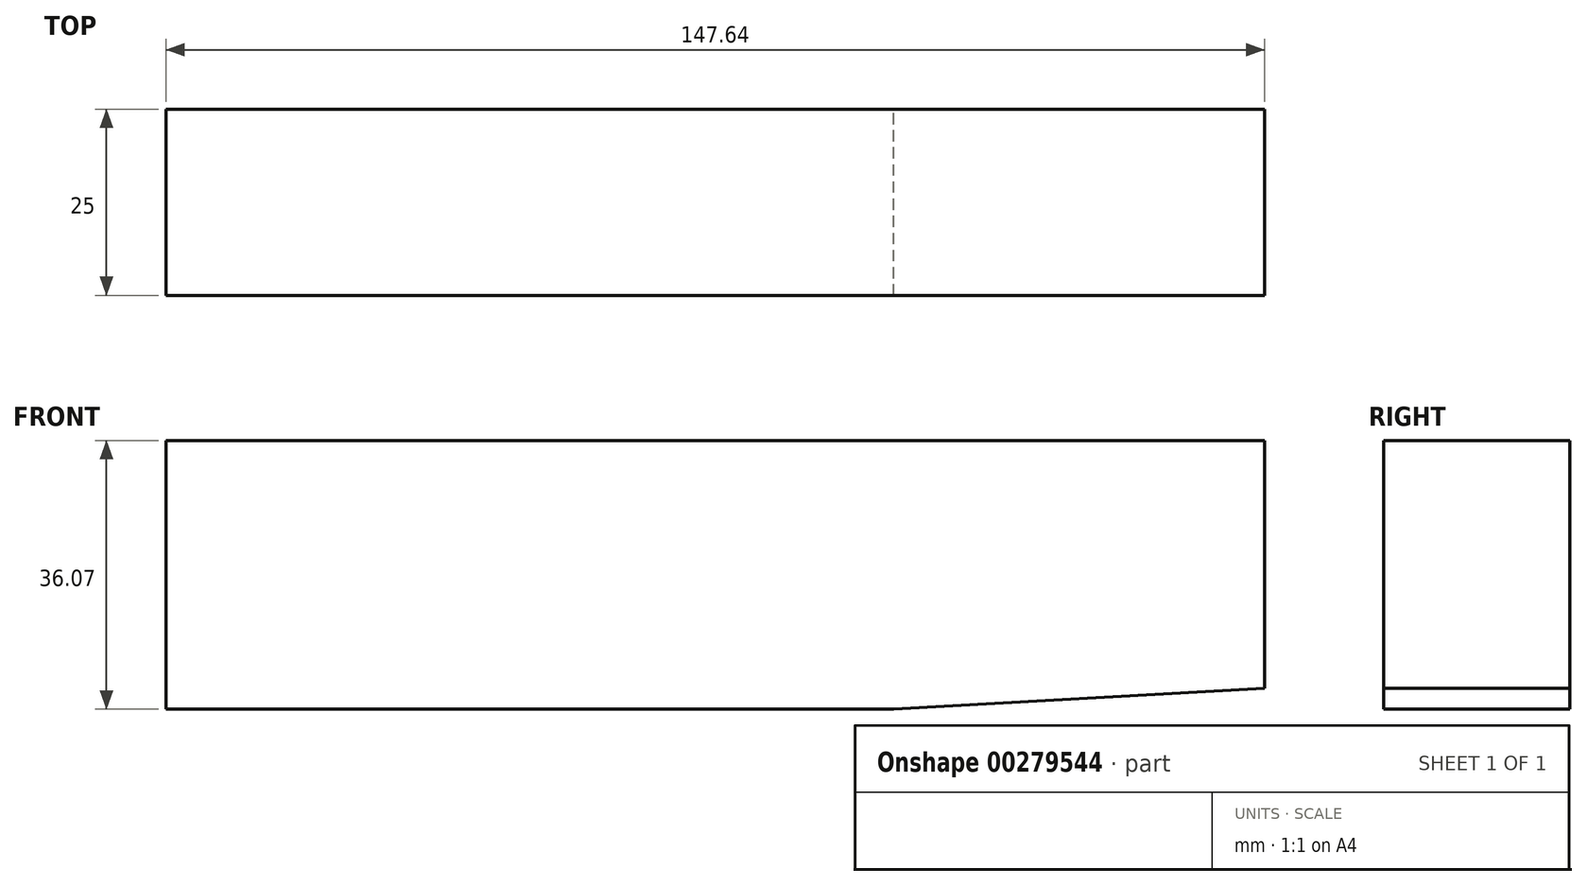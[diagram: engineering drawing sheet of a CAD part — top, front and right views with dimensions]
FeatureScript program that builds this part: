
annotation { "Feature Type Name" : "Feature", "Feature Type Description" : "" }
export const myFeature = defineFeature(function(context is Context, id is Id, definition is map)
    precondition{}
    {
        {
            var Q0;
            Q0=qCreatedBy(makeId("Front.planeOp"),FACE);
            var sketch = newSketch(context, id + "F0", { "sketchPlane" : qUnion([Q0])});
            skLineSegment(sketch, "E0", {"start": v(-10.57, 42.69) * mm, "end": v(40.71, 42.69) * mm});
            skLineSegment(sketch, "E1", {"start": v(40.71, 42.69) * mm, "end": v(40.71, 9.44) * mm});
            skLineSegment(sketch, "E2", {"start": v(40.71, 9.44) * mm, "end": v(-9.16, 6.62) * mm});
            skLineSegment(sketch, "E3", {"start": v(-9.16, 6.62) * mm, "end": v(-9.16, 42.69) * mm});
            skSolve(sketch);
        }
        {
            var Q0;
            {var subQ0=sQuery(id+"F0.wireOp",EDGE,"E1");Q0=makeQuery(id+"F0.imprint","IMPRINT",FACE,{"disambiguationData":[TD([[makeQuery(id+"F0.imprint","IMPRINT",EDGE,{"derivedFrom":subQ0}),-1.0]])]});}
            extrude(context, id + "F1", {"entities" : qUnion([Q0]), "depth" : 25 * mm});
        }
        {
            var Q0;
            Q0=makeQuery(id+"F1.opExtrude","CAP_FACE",FACE,{"disambiguationData":[OSD([sQuery(id+"F0.wireOp",EDGE,"E0"),sQuery(id+"F0.wireOp",EDGE,"E1"),sQuery(id+"F0.wireOp",EDGE,"E2"),sQuery(id+"F0.wireOp",EDGE,"E3")])],"isStart":false});
            var sketch = newSketch(context, id + "F2", { "sketchPlane" : qUnion([Q0])});
            skLineSegment(sketch, "E4", {"start": v(-9.16, 6.62) * mm, "end": v(-106.93, 6.62) * mm});
            skLineSegment(sketch, "E5", {"start": v(-106.93, 6.62) * mm, "end": v(-106.93, 42.69) * mm});
            skLineSegment(sketch, "E6", {"start": v(-106.93, 42.69) * mm, "end": v(-9.16, 42.69) * mm});
            skLineSegment(sketch, "E7", {"start": v(-9.16, 42.69) * mm, "end": v(-9.16, 6.62) * mm});
            skSolve(sketch);
        }
        {
            var Q0;
            Q0=makeQuery(id+"F2.imprint","IMPRINT",FACE,{"disambiguationData":[TD([[makeQuery(id+"F2.imprint","IMPRINT",EDGE,{"derivedFrom":sQuery(id+"F2.wireOp",EDGE,"E4")}),-1.0]])]});
            var Q1;
            Q1=makeQuery(id+"F1.opExtrude","CAP_VERTEX",VERTEX,{"disambiguationData":[OSD([sQuery(id+"F0.wireOp",EDGE,"E0"),sQuery(id+"F0.wireOp",EDGE,"E3")])],"isStart":true});
            extrude(context, id + "F3", {"entities" : qUnion([Q0]), "operationType" : NewBodyOperationType.ADD, "endBound" : BoundingType.UP_TO_VERTEX, "oppositeDirection" : true, "endBoundEntityVertex" : qUnion([Q1]), "depth" : 25 * mm});
        }
    });
